# Revit family: 2
name_source: partatom
category: Pipe Accessories
revit_build: Autodesk Revit 2018 (Build: 20190510_1515(x64)
units: mm (PartAtom-declared; Revit-internal decimal feet)

## family parameters
Always vertical = No
Cut with Voids When Loaded = No
OmniClass Number = 23.65.00.00
OmniClass Title = Supply and Distribution of Liquids and Gases
Part Type = Normal
Round Connector Dimension = Use Diameter
Shared = No
Work Plane-Based = No

## types (1)
- Defauly - please load Revit Family Type Catalog
    1/2 = Yes
    1/2 & 582L = Yes
    3/4 = No
    582L = No
    A = 57 mm
    Antifreeze: = Passiveted Propylene Glycol
    Application fluids = Water or glycol solutions-Air
    B = 30 mm  [stored 0.0984252 ft]
    BIMobject category = HVAC: Other HVAC
    Body Material = Pintossi - Metal - Brass CW617N
    Brand url = http://www.pintossi.it
    C = 22 mm
    Certifications = WRAS
    Closing tolerance = 20%
    Conditioning: = as indicated by the producer
    Copper (CU): = < 0,1 mg/kg (< 0,05 mg/kg for steam)
    D = 36 mm
    Description = Pintossi+C safety relief valve is designed in order to open automatically when the internal pressure of the system exceeds a pre-set maximum pressure value, by discharging the fluid throught it. Once the pressure of the system returns below the pre-set maximum value the safety valve closes automatically. This safety feature prevents reaching dangerous pressure levels which may damage and affect the components installed in the system.

Thanks to the ergonomic handwheel the valve can be manually open anytime, for checking the correct functioning

Pintossi+C safety relief valves are designed in compliance with the essential safety requirements stipulated in the EU Pressure Equipment Directive PED 2014/68/EU (Pressure Equipment Directive) and marked with CE logo. WRAS certified.

Available with manomter gauge art.584
    Design country = Italy
    E = 31 mm
    Edition number = 1
    Fluid aspect: = Limpid
    Height Connector = 9 mm  [stored 0.0295276 ft]
    IFC Classification = Valve
    Inlet/Outlet Diameter = 13 mm
    Iron (FE): = < 0,5 mg/kg (< 0,1 mg/kg for steam)
    Length Connector = 30 mm  [stored 0.0984252 ft]
    Main Inlet/Outlet Diameter = 13 mm
    Manufacturer = Pintossi+c
    Manufacturer country = Italy
    Manufacturer name = Pintossi+c
    Masterformat 2014 Code = 23 00 00
    Masterformat 2014 Description = Heating, Ventilating, and Air Conditioning (HVAC)
    Material main = Brass
    Maximum percentage of glycol [%] = 30
    Maximum working pressure = 10.0 bar
    Maximum working temperature = 100 °C
    Model = 582
    NBS Reference Code = 94-94-xx
    NBS Reference Description = Safety Valves
    Opening overpressure = 10%
    PH: = Between 7 and 8
    Pressure of setting = 1.5 bar
    Product Guid = 872120b0-4eb1-4027-9c92-c774404f5cc9
    Product data url = https://www.bimobject.com
    Product family = Components for central heating systems
    Product group = Safety valves
    Tolerance = 10% for valves with pre-set pressure <5bar. 0,5 bar for valves with pre-set pressure >5bar
    UNSPSC Code = 401416
    URL = www.pintossi.it
    Uniclass 1.4 Code = JT
    Uniclass 1.4 Description = Mechanical heating, cooling and refrigeration systems
    Uniclass 2.0 Code = PR-94-94-xx
    Uniclass 2.0 Description = Safety Valves
    Uniclass 2015 Code = Pr_65_54_95_75
    Uniclass 2015 Name = Safety valves
    Uniformat II Code = D30
    Uniformat II Description = HVAC
    Wheelhandle Material = Pintossi - Plastic - Red

note: [stored X ft] marks values corroborated as IEEE doubles in the binary element streams (Revit-internal decimal feet)

## geometry (parser evidence)
native form markers: Sweep x2
no freeform markers — native parametric forms only
